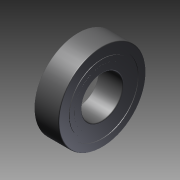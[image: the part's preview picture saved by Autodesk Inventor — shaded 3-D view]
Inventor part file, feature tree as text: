
AUTODESK INVENTOR PART (.ipt)
format: ipt  version: 2011 SP1 (Build 150282100, 282)  size: 156,160 bytes
history: native  units: mm
features: other x7, revolve x3, sketch x3
ambient origin geometry x8: Origin, YZ Plane, XZ Plane, XY Plane, X Axis, Y Axis, Z Axis, Center Point
bodies: Solid1 (feature_tree)
feature tree (13):
  revolve  "Revolution1"  Angle=360.0deg
  revolve  "Revolution2"  [1 undecoded]
  revolve  "Revolution3"  [1 undecoded]
  other  "bf_2_XY"
  other  "bf_2_YZ"
  other  "bf_2_ZX"
  other  "bf_2_X"
  other  "bf_2_Y"
  other  "bf_2_Z"
  other  "bf_2_Center"
  sketch  "Sketch_1"  dims[d0=360.0deg d1=360.0deg]
  sketch  "Sketch_2"  dims[d2=360.0deg]
  sketch  "Sketch_3"
note: 2 required parameter values undecoded (feature->parameter linkage not recoverable at this tier; creation-order binding heuristic only, values carry confidence <= 0.55)
